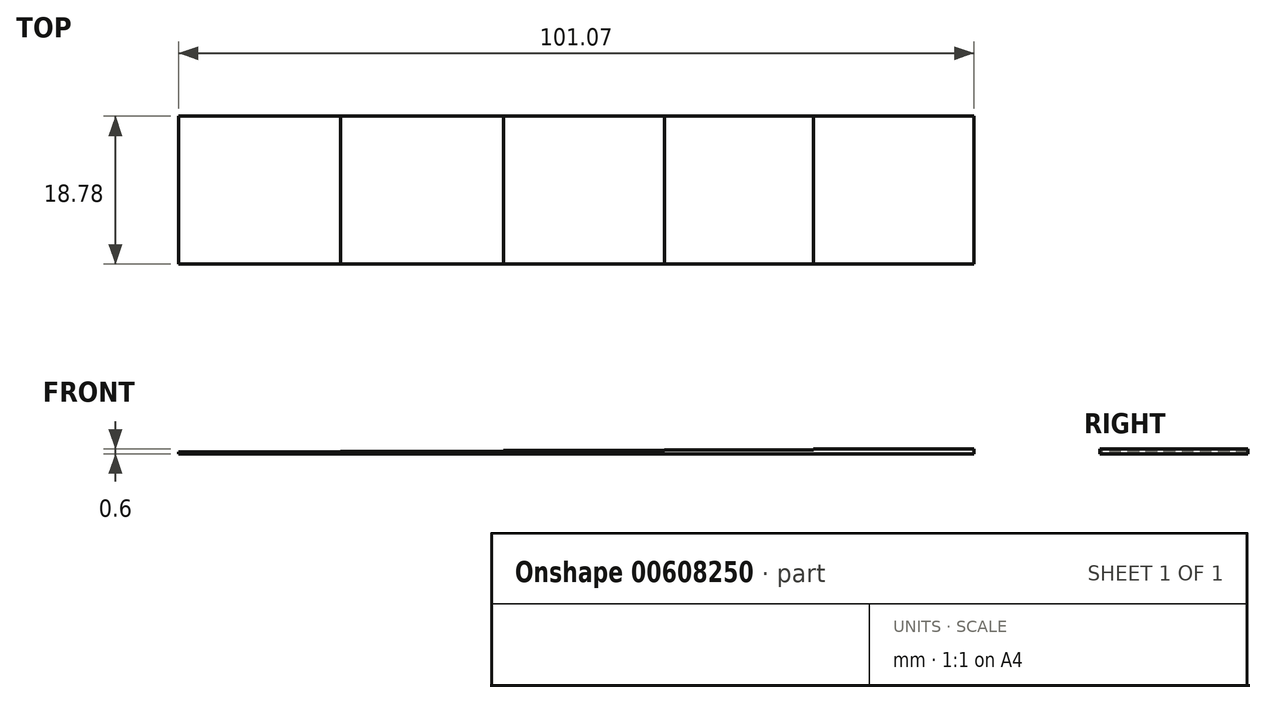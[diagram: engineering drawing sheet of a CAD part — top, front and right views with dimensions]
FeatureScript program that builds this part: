
annotation { "Feature Type Name" : "Feature", "Feature Type Description" : "" }
export const myFeature = defineFeature(function(context is Context, id is Id, definition is map)
    precondition{}
    {
        {
            var Q0;
            Q0=qCreatedBy(makeId("Top.planeOp"),FACE);
            var sketch = newSketch(context, id + "F0", { "sketchPlane" : qUnion([Q0])});
            skLineSegment(sketch, "E0.bottom", {"start": v(0, 0) * mm, "end": v(20.58, 0) * mm});
            skLineSegment(sketch, "E0.top", {"start": v(0, -18.78) * mm, "end": v(20.58, -18.78) * mm});
            skLineSegment(sketch, "E0.left", {"start": v(0, 0) * mm, "end": v(0, -18.78) * mm});
            skLineSegment(sketch, "E0.right", {"start": v(20.58, 0) * mm, "end": v(20.58, -18.78) * mm});
            skLineSegment(sketch, "E1.bottom", {"start": v(20.58, 0) * mm, "end": v(41.31, 0) * mm});
            skLineSegment(sketch, "E1.top", {"start": v(20.58, -18.78) * mm, "end": v(41.31, -18.78) * mm});
            skLineSegment(sketch, "E1.right", {"start": v(41.31, 0) * mm, "end": v(41.31, -18.78) * mm});
            skLineSegment(sketch, "E2.bottom", {"start": v(41.31, 0) * mm, "end": v(61.74, 0) * mm});
            skLineSegment(sketch, "E2.top", {"start": v(41.31, -18.78) * mm, "end": v(61.74, -18.78) * mm});
            skLineSegment(sketch, "E2.right", {"start": v(61.74, 0) * mm, "end": v(61.74, -18.78) * mm});
            skLineSegment(sketch, "E3.bottom", {"start": v(61.74, 0) * mm, "end": v(80.67, 0) * mm});
            skLineSegment(sketch, "E3.top", {"start": v(61.74, -18.78) * mm, "end": v(80.67, -18.78) * mm});
            skLineSegment(sketch, "E3.right", {"start": v(80.67, 0) * mm, "end": v(80.67, -18.78) * mm});
            skLineSegment(sketch, "E4.bottom", {"start": v(80.67, 0) * mm, "end": v(101.07, 0) * mm});
            skLineSegment(sketch, "E4.top", {"start": v(80.67, -18.78) * mm, "end": v(101.07, -18.78) * mm});
            skLineSegment(sketch, "E4.right", {"start": v(101.07, 0) * mm, "end": v(101.07, -18.78) * mm});
            skSolve(sketch);
        }
        {
            var Q0;
            Q0=makeQuery(id+"F0.imprint","IMPRINT",FACE,{"disambiguationData":[TD([[makeQuery(id+"F0.imprint","IMPRINT",EDGE,{"derivedFrom":sQuery(id+"F0.wireOp",EDGE,"E0.bottom")}),-1.0]])]});
            extrude(context, id + "F1", {"entities" : qUnion([Q0]), "depth" : 0.2 * mm, "offsetDistance" : 25 * mm});
        }
        {
            var Q0;
            Q0=makeQuery(id+"F0.imprint","IMPRINT",FACE,{"disambiguationData":[TD([[makeQuery(id+"F0.imprint","IMPRINT",EDGE,{"derivedFrom":sQuery(id+"F0.wireOp",EDGE,"E1.bottom")}),-1.0]])]});
            extrude(context, id + "F2", {"entities" : qUnion([Q0]), "operationType" : NewBodyOperationType.ADD, "depth" : 0.3 * mm, "offsetDistance" : 25 * mm});
        }
        {
            var Q0;
            Q0=makeQuery(id+"F0.imprint","IMPRINT",FACE,{"disambiguationData":[TD([[makeQuery(id+"F0.imprint","IMPRINT",EDGE,{"derivedFrom":sQuery(id+"F0.wireOp",EDGE,"E2.bottom")}),-1.0]])]});
            extrude(context, id + "F3", {"entities" : qUnion([Q0]), "operationType" : NewBodyOperationType.ADD, "depth" : .4 * mm, "offsetDistance" : 25 * mm});
        }
        {
            var Q0;
            Q0=makeQuery(id+"F0.imprint","IMPRINT",FACE,{"disambiguationData":[TD([[makeQuery(id+"F0.imprint","IMPRINT",EDGE,{"derivedFrom":sQuery(id+"F0.wireOp",EDGE,"E3.bottom")}),-1.0]])]});
            extrude(context, id + "F4", {"entities" : qUnion([Q0]), "operationType" : NewBodyOperationType.ADD, "depth" : 0.5 * mm, "offsetDistance" : 25 * mm});
        }
        {
            var Q0;
            Q0=makeQuery(id+"F0.imprint","IMPRINT",FACE,{"disambiguationData":[TD([[makeQuery(id+"F0.imprint","IMPRINT",EDGE,{"derivedFrom":sQuery(id+"F0.wireOp",EDGE,"E4.bottom")}),-1.0]])]});
            extrude(context, id + "F5", {"entities" : qUnion([Q0]), "operationType" : NewBodyOperationType.ADD, "depth" : .6 * mm, "offsetDistance" : 25 * mm});
        }
    });
